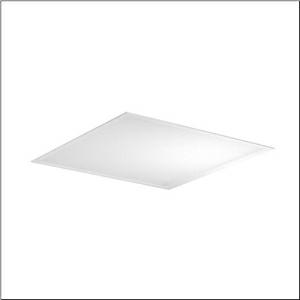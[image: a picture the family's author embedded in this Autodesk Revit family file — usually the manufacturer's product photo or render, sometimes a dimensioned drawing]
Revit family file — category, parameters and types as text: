
# Revit family: apollon_r__31_square_51mp12w72442_a98a
name_source: partatom
category: Lighting Fixtures
units: mm (PartAtom-declared; Revit-internal decimal feet)

## family parameters
Cut with Voids When Loaded = No
Host = Face
Light Source = No
Part Type = Normal
Room Calculation Point = No
Round Connector Dimension = Use Diameter
Shared = No

## types (1)
- Apollon® 31 square (1 x LED, 4000 lm, 27.5 W, 4000K)
    Apparent Load = 28 VA
    CIE Flux Codes = 61 87 97 100 100
    Color Rendering = 80
    Color Temperature = 4000K
    Default Elevation = 1800 mm
    Description = Apollon® 31 square, office luminaire, primary optical cover: micro prismatic cover, of PMMA, CAT 2 (L<= 3000cd/m²), light emission: direct distribution, primary light characteristic: symmetric, installation type: lay-in mounting, LED, rated luminous flux: 4.000lm, luminous efficacy: 145lm/W, light colour: 840, colour temperature: 4000K, control gear: ON/OFF, with terminal, 3-pole, mains connection: 220..240V, AC, 50/60Hz, rated input power: 28W, housing, of aluminium, traffic white (RAL 9016), module: M600, length: 595mm, width: 595mm, height: 62mm, recess depth: 180mm, housing upper side, of sheet steel, coated, protection rating (complete): IP20, protection rating (on room side): IP40, insulation class (complete): insulation class II (safety insulation), certification: CE, ENEC, impact resistance: IK03, permissible operating ambient temperature: -20..+40°C, permissible storage temperature: -20..+60°C, packaging unit: 1 piece
    Height = 0 mm  [stored 0 ft]
    Lamp = 1 x LED
    Lamp Light Flux = 4000 lm
    Lamp Power = 27.5 W
    Lamp count = 1
    Length = 595 mm
    Luminous efficacy = 145 lm/W
    Manufacturer = Siteco
    ModVariant = No
    Model = 51MP12W72442
    Mounting Place = Ceiling
    Mounting Type = Recessed
    Number of Poles = 1
    OnlyDefault = Yes
    Power Factor = 1
    Product Name = Apollon® 31 square
    Product group = office luminaire | ceiling recessed
    ProductGroupID = 401
    Protection Class = Protection class II
    Protection Degree = IP 20
    RLX_Detail_Level = 1
    RLX_Emergency_Light_Flux = 0 lm
    RLX_Emergency_Type = 0
    RLX_Emergency_Type_DB = No
    RlxData = <blob elided: 12533 chars, md5=f276d410>
    Socket = socket
    Standby Power = 0 W
    System Light Flux = 4000 lm
    System Power = 28 W
    Type Comments = Product without accessories
    Type Image = l_1291035.jpg
    URL = http://relux.com
    VarID = ---
    Voltage = 0 V
    Weight = 0.00 kg
    Width = 595 mm

note: [stored X ft] marks values corroborated as IEEE doubles in the binary element streams (Revit-internal decimal feet)

## geometry (parser evidence)
native form markers: Sweep x9
no freeform markers — native parametric forms only
